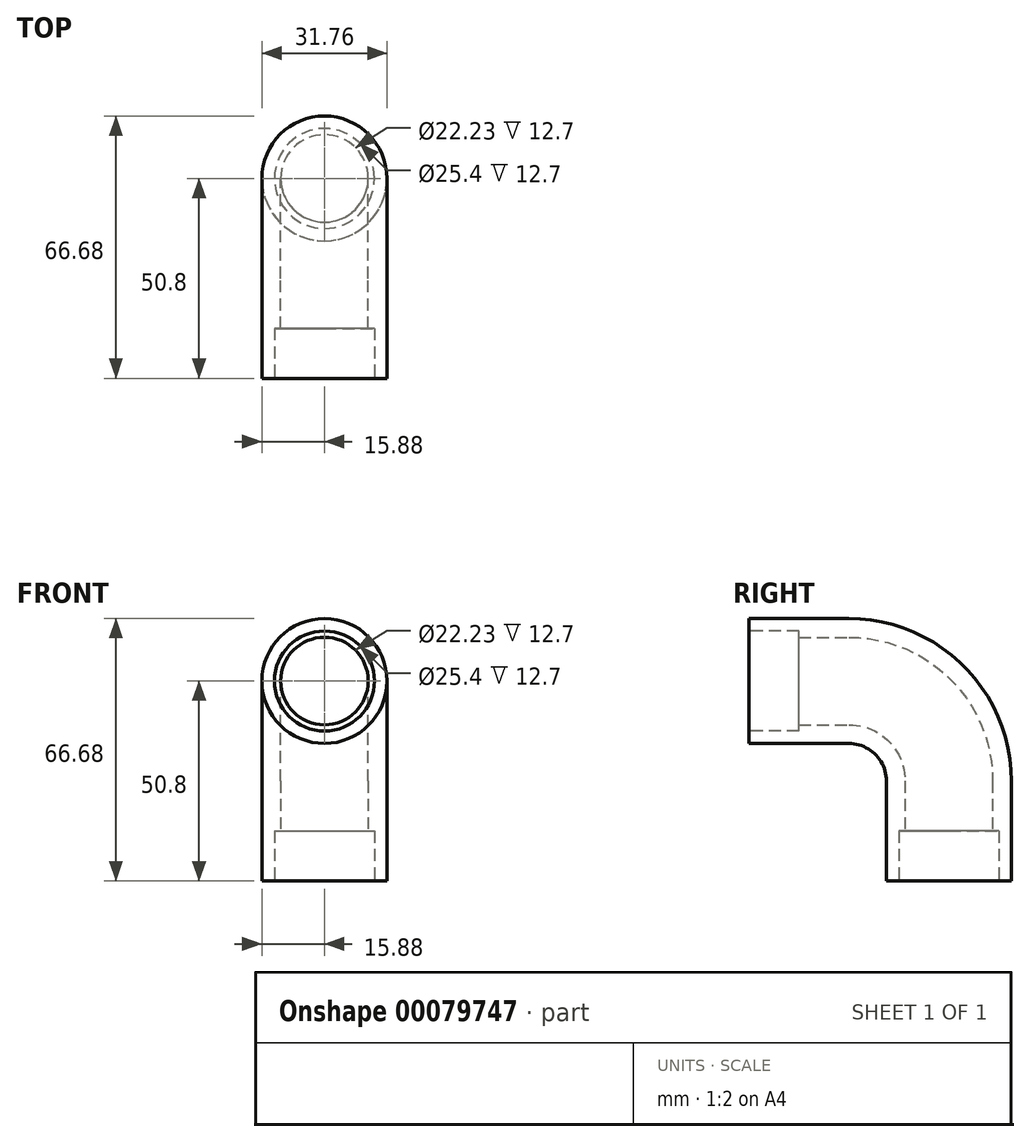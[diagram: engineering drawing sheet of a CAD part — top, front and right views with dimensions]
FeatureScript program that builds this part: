
annotation { "Feature Type Name" : "Feature", "Feature Type Description" : "" }
export const myFeature = defineFeature(function(context is Context, id is Id, definition is map)
    precondition{}
    {
        {
            var Q0;
            Q0=qCreatedBy(makeId("Front.planeOp"),FACE);
            var sketch = newSketch(context, id + "F0", { "sketchPlane" : qUnion([Q0])});
            skCircle(sketch, "E0", {"center": v(0, 0) * mm, "radius": 15.88 * mm});
            skCircle(sketch, "E1", {"center": v(0, 0) * mm, "radius": 11.11 * mm});
            skSolve(sketch);
        }
        {
            var Q0;
            Q0=qCreatedBy(makeId("Right.planeOp"),FACE);
            var sketch = newSketch(context, id + "F1", { "sketchPlane" : qUnion([Q0])});
            skLineSegment(sketch, "E2", {"start": v(0, 0) * mm, "end": v(25.4, 0) * mm});
            skLineSegment(sketch, "E3", {"start": v(50.8, -25.4) * mm, "end": v(50.8, -50.8) * mm});
            skPoint(sketch, "E4.visualSharp", {"position": v(50.8, 0) * mm});
            skArc(sketch, "E4.filletArc", {"start": v(50.8, -25.4) * mm, "mid": v(43.36, -7.44) * mm, "end": v(25.4, 0) * mm});
            skSolve(sketch);
        }
        {
            var Q0;
            Q0=makeQuery(id+"F0.imprint","IMPRINT",FACE,{"disambiguationData":[TD([[makeQuery(id+"F0.imprint","IMPRINT",EDGE,{"derivedFrom":sQuery(id+"F0.wireOp",EDGE,"E0")}),1.0]])]});
            var Q1;
            Q1=sQuery(id+"F1.wireOp",EDGE,"E2");
            var Q2;
            Q2=sQuery(id+"F1.wireOp",EDGE,"E4.filletArc");
            var Q3;
            Q3=sQuery(id+"F1.wireOp",EDGE,"E3");
            sweep(context, id + "F2", {"profiles" : qUnion([Q0]), "path" : qUnion([Q1, Q2, Q3])});
        }
        {
            var Q0;
            Q0=makeQuery(id+"F0.imprint","IMPRINT",FACE,{"disambiguationData":[TD([[makeQuery(id+"F0.imprint","IMPRINT",EDGE,{"derivedFrom":sQuery(id+"F0.wireOp",EDGE,"E1")}),1.0]])]});
            var sketch = newSketch(context, id + "F3", { "sketchPlane" : qUnion([Q0])});
            skCircle(sketch, "E5", {"center": v(0, 0) * mm, "radius": 12.7 * mm});
            skSolve(sketch);
        }
        {
            var Q0;
            Q0 = qSketchRegion(id + "F3", true);
            extrude(context, id + "F4", {"entities" : qUnion([Q0]), "operationType" : NewBodyOperationType.REMOVE, "oppositeDirection" : true, "depth" : 12.7 * mm});
        }
        {
            var Q0;
            Q0=makeQuery(id+"F2.opSweep","CAP_FACE",FACE,{"disambiguationData":[OSD([sQuery(id+"F0.wireOp",EDGE,"E0"),sQuery(id+"F0.wireOp",EDGE,"E1"),sQuery(id+"F1.wireOp",VERTEX,"E3.end")])],"isStart":false});
            var sketch = newSketch(context, id + "F5", { "sketchPlane" : qUnion([Q0])});
            skCircle(sketch, "E6", {"center": v(0, -50.8) * mm, "radius": 12.7 * mm});
            skSolve(sketch);
        }
        {
            var Q0;
            Q0 = qSketchRegion(id + "F5", true);
            extrude(context, id + "F6", {"entities" : qUnion([Q0]), "operationType" : NewBodyOperationType.REMOVE, "oppositeDirection" : true, "depth" : 12.7 * mm});
        }
    });
